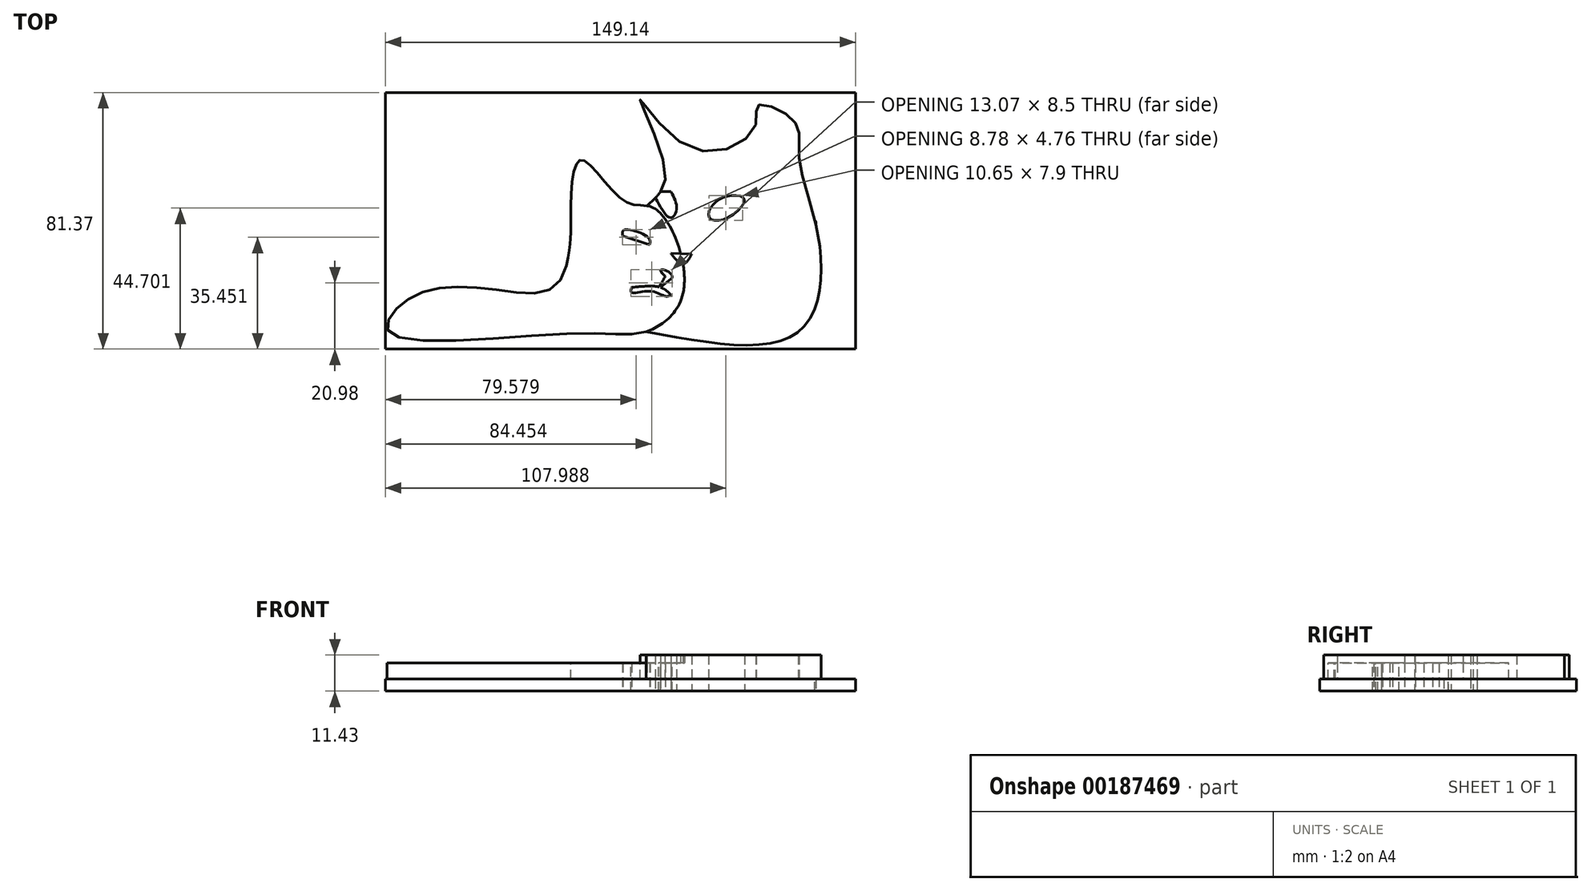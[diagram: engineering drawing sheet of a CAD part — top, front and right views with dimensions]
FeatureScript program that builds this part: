
annotation { "Feature Type Name" : "Feature", "Feature Type Description" : "" }
export const myFeature = defineFeature(function(context is Context, id is Id, definition is map)
    precondition{}
    {
        {
            var Q0;
            Q0=qCreatedBy(makeId("Top.planeOp"),FACE);
            var sketch = newSketch(context, id + "F0", { "sketchPlane" : qUnion([Q0])});
            skFitSpline(sketch, "E0", {"points": [v(-70.48, -21.87) * mm, v(-58.62, -14.3) * mm, v(-37.43, -14.3) * mm, v(-19.35, -13.51) * mm, v(-14.3, -1.46) * mm, v(-13.9, 8.07) * mm, v(-10.8, 26.93) * mm, v(3.01, 13.9) * mm, v(12.93, 11.37) * mm, v(21.87, -14.49) * mm, v(10.01, -27.51) * mm, v(-10.6, -28.1) * mm, v(-70.87, -28.3) * mm, v(-70.48, -21.87) * mm]});
            skFitSpline(sketch, "E1", {"points": [v(-15.3, -6.58) * mm, v(-7.6, -14.52) * mm, v(0, -14.75) * mm, v(9.97, -17.06) * mm, v(21.87, -14.49) * mm], "startDerivative": vector(27.98, -39.88) * mm, "endDerivative": vector(44.35, 15.83) * mm});
            skFitSpline(sketch, "E2", {"points": [v(2.57, 2.82) * mm, v(11.12, 0) * mm], "startDerivative": vector(8.56, -2.82) * mm, "endDerivative": vector(8.56, -2.82) * mm});
            skFitSpline(sketch, "E3", {"points": [v(12.93, 14.85) * mm, v(15.98, 23.63) * mm, v(8.12, 46.06) * mm, v(24.53, 30.57) * mm, v(44.65, 37.74) * mm, v(45.34, 44.21) * mm, v(54.36, 41.44) * mm, v(58.52, 35.42) * mm, v(58.52, 26.93) * mm, v(65, 0) * mm, v(57.83, -27.93) * mm, v(10.01, -27.51) * mm], "startDerivative": vector(82.82, 92.4) * mm, "endDerivative": vector(-384.02, 73.11) * mm});
            skFitSpline(sketch, "E4", {"points": [v(26.15, -14.49) * mm, v(63.46, 7.76) * mm, v(63.79, 6.39) * mm], "startDerivative": vector(61.67, 41.15) * mm, "endDerivative": vector(-0.84, -11.62) * mm});
            skFitSpline(sketch, "E5", {"points": [v(23.6, -14.49) * mm, v(26.15, -14.49) * mm], "startDerivative": vector(2.54, 0) * mm, "endDerivative": vector(2.54, 0) * mm});
            skFitSpline(sketch, "E6", {"points": [v(17.83, 16.88) * mm, v(14.76, 16.88) * mm], "startDerivative": vector(-3.08, 0) * mm, "endDerivative": vector(-3.08, 0) * mm});
            skFitSpline(sketch, "E7", {"points": [v(17.83, 16.88) * mm, v(19.68, 11.37) * mm, v(17.83, 8.6) * mm, v(12.93, 14.85) * mm], "startDerivative": vector(8.8, -16.19) * mm, "endDerivative": vector(-13.05, 23.6) * mm});
            skFitSpline(sketch, "E8", {"points": [v(14.36, 14.85) * mm, v(16.8, 14.85) * mm], "startDerivative": vector(2.45, 0) * mm, "endDerivative": vector(2.45, 0) * mm});
            skFitSpline(sketch, "E9", {"points": [v(30.08, 8.6) * mm, v(35.4, 8.37) * mm, v(41.18, 14.38) * mm, v(36.56, 15.54) * mm, v(31, 12.53) * mm, v(30.08, 8.6) * mm]});
            skFitSpline(sketch, "E10", {"points": [v(24.46, -2.96) * mm, v(21.7, -6.1) * mm, v(17.83, -2.73) * mm], "startDerivative": vector(-5.43, -9.68) * mm, "endDerivative": vector(-7.77, 9.8) * mm});
            skFitSpline(sketch, "E11", {"points": [v(17.83, -2.73) * mm, v(24.46, -2.96) * mm], "startDerivative": vector(6.62, -0.23) * mm, "endDerivative": vector(6.62, -0.23) * mm});
            skFitSpline(sketch, "E12", {"points": [v(14.59, -8.05) * mm, v(17.83, -10.82) * mm, v(17.83, -9.2) * mm, v(14.59, -8.05) * mm]});
            skFitSpline(sketch, "E13", {"points": [v(30.08, -9.2) * mm, v(24.46, -9.2) * mm], "startDerivative": vector(-5.63, 0) * mm, "endDerivative": vector(-5.63, 0) * mm});
            skFitSpline(sketch, "E14", {"points": [v(5.42, -13.51) * mm, v(14.59, -13.51) * mm, v(17.83, -15.93) * mm], "startDerivative": vector(17.4, 1.82) * mm, "endDerivative": vector(6.7, -7.26) * mm});
            skFitSpline(sketch, "E15", {"points": [v(17.83, -10.82) * mm, v(14.59, -13.51) * mm], "startDerivative": vector(-3.24, -2.7) * mm, "endDerivative": vector(-3.24, -2.7) * mm});
            skFitSpline(sketch, "E16", {"points": [v(22.25, -9.2) * mm, v(21.7, -6.1) * mm], "startDerivative": vector(-0.56, 3.11) * mm, "endDerivative": vector(-0.56, 3.11) * mm});
            skFitSpline(sketch, "E17", {"points": [v(33.12, 14.38) * mm, v(36.56, 12.53) * mm, v(36.56, 12.07) * mm], "startDerivative": vector(6.33, -2.74) * mm, "endDerivative": vector(-0.6, -1.72) * mm});
            skLineSegment(sketch, "E18.bottom", {"start": v(-72.72, 48.3) * mm, "end": v(76.42, 48.3) * mm});
            skLineSegment(sketch, "E18.top", {"start": v(-72.72, -33.07) * mm, "end": v(76.42, -33.07) * mm});
            skLineSegment(sketch, "E18.left", {"start": v(-72.72, 48.3) * mm, "end": v(-72.72, -33.07) * mm});
            skLineSegment(sketch, "E18.right", {"start": v(76.42, 48.3) * mm, "end": v(76.42, -33.07) * mm});
            skLineSegment(sketch, "E19", {"start": v(12.93, 14.85) * mm, "end": v(10.21, 12.37) * mm});
            skLineSegment(sketch, "E20", {"start": v(23.6, -14.49) * mm, "end": v(21.87, -14.49) * mm});
            skFitSpline(sketch, "E21", {"points": [v(2.57, 2.82) * mm, v(2.97, 4.7) * mm, v(10.62, 2.35) * mm, v(11.12, 0) * mm], "startDerivative": vector(-1.68, 9.9) * mm, "endDerivative": vector(-1.8, -8.7) * mm});
            skFitSpline(sketch, "E22", {"points": [v(5.42, -13.51) * mm, v(5.42, -15.14) * mm, v(11.12, -14.68) * mm, v(16.27, -16.32) * mm, v(17.83, -15.93) * mm], "startDerivative": vector(-3.25, -11.79) * mm, "endDerivative": vector(7.93, 4.15) * mm});
            skFitSpline(sketch, "E23", {"points": [v(16.12, -9.95) * mm, v(13.94, -13.34) * mm, v(13.84, -13.32) * mm], "startDerivative": vector(-3.3, -5.7) * mm, "endDerivative": vector(-0.62, 0.4) * mm});
            skLineSegment(sketch, "E24", {"start": v(14.4, 14.68) * mm, "end": v(14.76, 14.04) * mm});
            skLineSegment(sketch, "E25", {"start": v(14.76, 14.04) * mm, "end": v(16.8, 14.85) * mm});
            skLineSegment(sketch, "E26", {"start": v(14.76, 16.88) * mm, "end": v(14.6, 16.88) * mm});
            skLineSegment(sketch, "E27", {"start": v(14.4, 14.68) * mm, "end": v(14.36, 14.85) * mm});
            skSolve(sketch);
        }
        {
            var Q0;
            Q0=makeQuery(id+"F0.imprint","IMPRINT",FACE,{"disambiguationData":[TD([[makeQuery(id+"F0.imprint","IMPRINT",EDGE,{"derivedFrom":sQuery(id+"F0.wireOp",EDGE,"E18.bottom")}),-1.0]])]});
            extrude(context, id + "F1", {"entities" : qUnion([Q0]), "depth" : 3.8 * mm});
        }
        {
            var Q0;
            Q0=makeQuery(id+"F0.imprint","IMPRINT",FACE,{"disambiguationData":[TD([[makeQuery(id+"F0.imprint","IMPRINT",EDGE,{"derivedFrom":sQuery(id+"F0.wireOp",EDGE,"E2")}),-1.0]])]});
            var Q1;
            {var subQ0=sQuery(id+"F0.wireOp",EDGE,"E1");var subQ1=sQuery(id+"F0.wireOp",EDGE,"E0");var subQ5=makeQuery(id+"F0.imprint","INTERSECT",VERTEX,{"derivedFrom":[subQ1,subQ0]});Q1=makeQuery(id+"F0.imprint","IMPRINT",FACE,{"disambiguationData":[TD([[makeQuery(id+"F0.imprint","IMPRINT",EDGE,{"disambiguationData":[TD([[subQ5,1.0]])],"derivedFrom":subQ1}),-1.0]])]});}
            extrude(context, id + "F2", {"entities" : qUnion([Q0, Q1]), "operationType" : NewBodyOperationType.ADD, "depth" : 8.9 * mm});
        }
        {
            var Q0;
            {var subQ5=sQuery(id+"F0.wireOp",EDGE,"E5");Q0=makeQuery(id+"F0.imprint","IMPRINT",FACE,{"disambiguationData":[TD([[makeQuery(id+"F0.imprint","IMPRINT",EDGE,{"derivedFrom":subQ5}),1.0]])]});}
            var Q1;
            {var subQ5=sQuery(id+"F0.wireOp",EDGE,"E5");Q1=makeQuery(id+"F0.imprint","IMPRINT",FACE,{"disambiguationData":[TD([[makeQuery(id+"F0.imprint","IMPRINT",EDGE,{"derivedFrom":subQ5}),-1.0]])]});}
            extrude(context, id + "F3", {"entities" : qUnion([Q0, Q1]), "operationType" : NewBodyOperationType.ADD, "depth" : 11.43 * mm});
        }
    });
